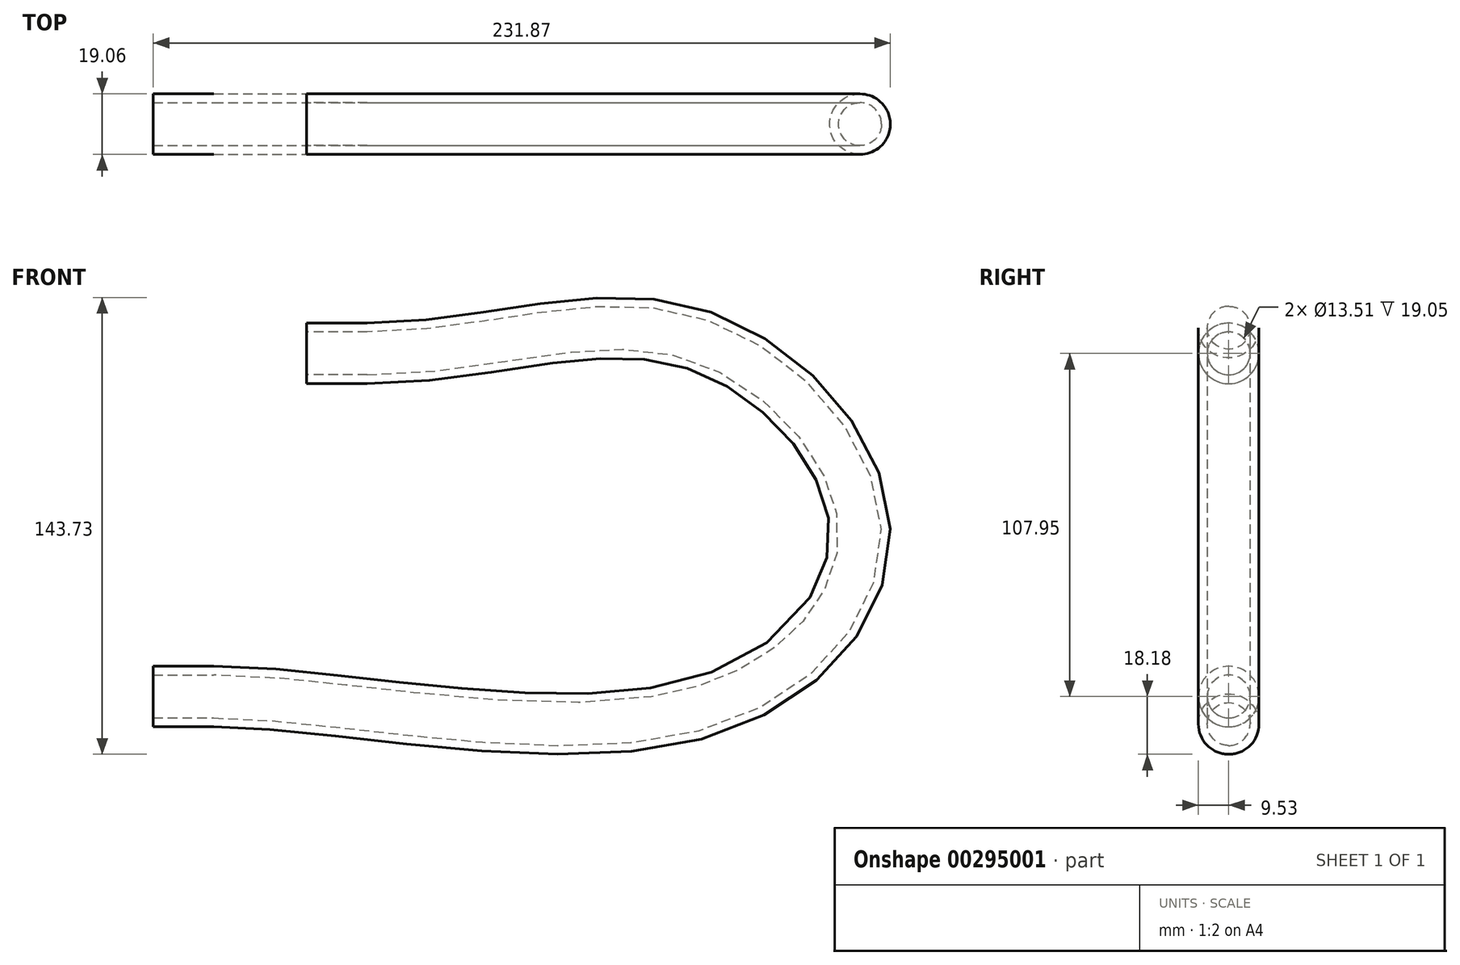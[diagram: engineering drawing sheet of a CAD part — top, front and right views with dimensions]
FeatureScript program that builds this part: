
annotation { "Feature Type Name" : "Feature", "Feature Type Description" : "" }
export const myFeature = defineFeature(function(context is Context, id is Id, definition is map)
    precondition{}
    {
        {
            var Q0;
            Q0=qCreatedBy(makeId("Front.planeOp"),FACE);
            var sketch = newSketch(context, id + "F0", { "sketchPlane" : qUnion([Q0])});
            skLineSegment(sketch, "E0", {"start": v(0, 0) * mm, "end": v(0, 107.95) * mm, "construction": true});
            skLineSegment(sketch, "E1", {"start": v(0, 107.95) * mm, "end": v(48.26, 107.95) * mm, "construction": true});
            skLineSegment(sketch, "E2", {"start": v(0, 0) * mm, "end": v(19.05, 0) * mm});
            skLineSegment(sketch, "E3", {"start": v(48.26, 107.95) * mm, "end": v(67.31, 107.95) * mm});
            skFitSpline(sketch, "E4", {"points": [v(19.05, 0) * mm, v(171.45, -3.81) * mm, v(222.25, 53.98) * mm, v(168.91, 113.03) * mm, v(67.31, 107.95) * mm], "startDerivative": vector(387.85, 0) * mm, "endDerivative": vector(-457.59, 0) * mm});
            skSolve(sketch);
        }
        {
            var Q0;
            Q0=qCreatedBy(makeId("Right.planeOp"),FACE);
            var sketch = newSketch(context, id + "F1", { "sketchPlane" : qUnion([Q0])});
            skCircle(sketch, "E5", {"center": v(0, 0) * mm, "radius": 6.76 * mm});
            skCircle(sketch, "E6", {"center": v(0, 0) * mm, "radius": 9.53 * mm});
            skSolve(sketch);
        }
        {
            var Q0;
            Q0=makeQuery(id+"F1.imprint","IMPRINT",FACE,{"disambiguationData":[TD([[makeQuery(id+"F1.imprint","IMPRINT",EDGE,{"derivedFrom":sQuery(id+"F1.wireOp",EDGE,"E5")}),-1.0]])]});
            var Q1;
            Q1=sQuery(id+"F0.wireOp",EDGE,"E2");
            var Q2;
            Q2=sQuery(id+"F0.wireOp",EDGE,"E4");
            var Q3;
            Q3=sQuery(id+"F0.wireOp",EDGE,"E3");
            sweep(context, id + "F2", {"profiles" : qUnion([Q0]), "path" : qUnion([Q1, Q2, Q3])});
        }
    });
